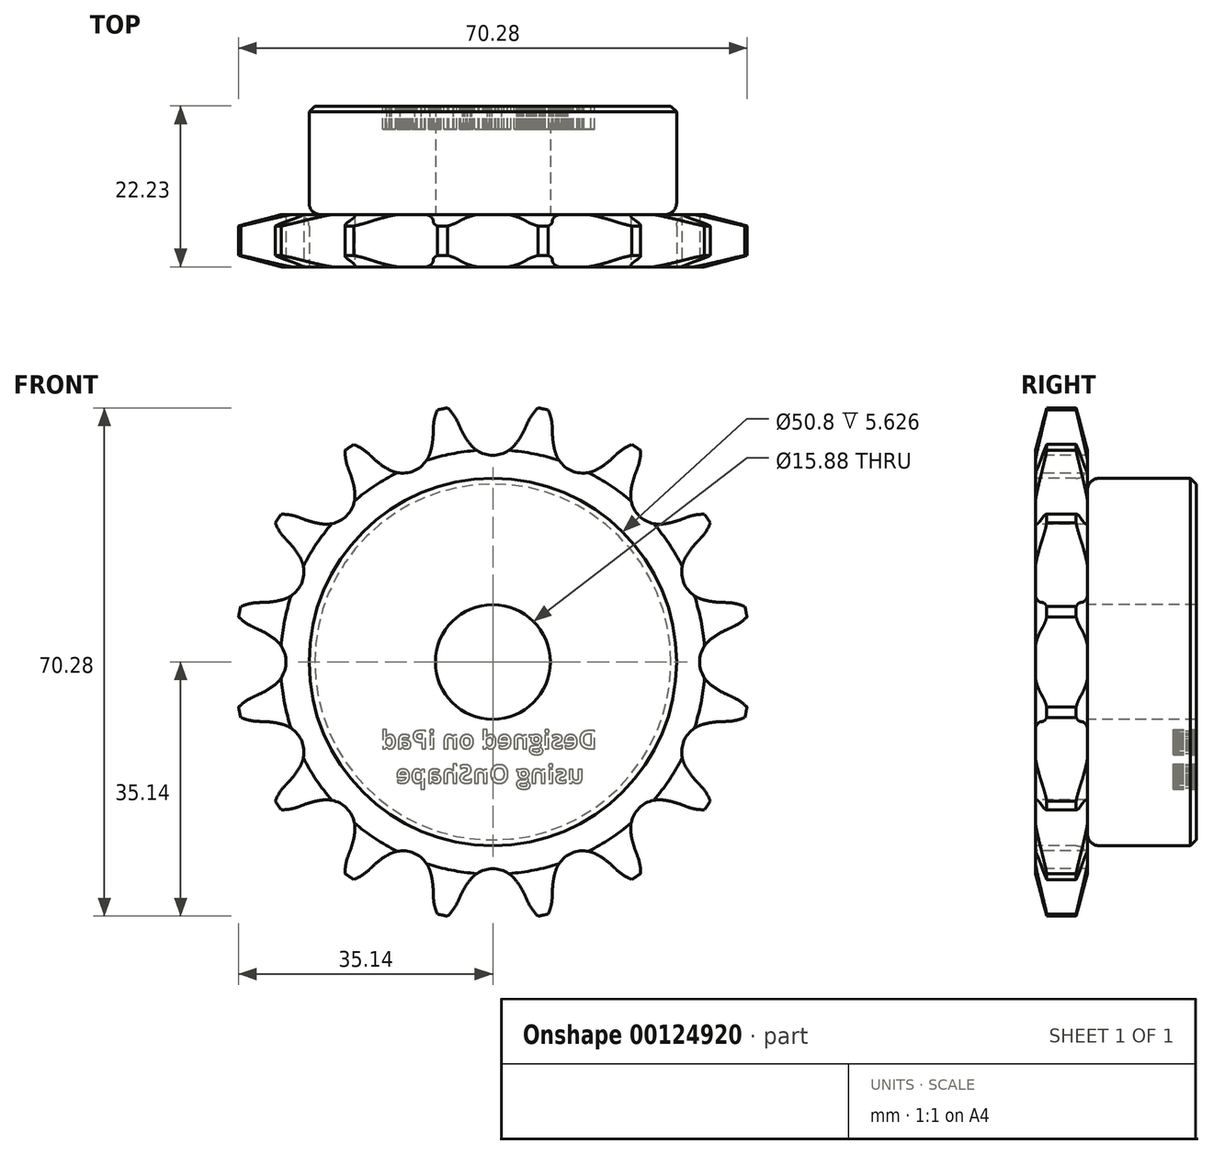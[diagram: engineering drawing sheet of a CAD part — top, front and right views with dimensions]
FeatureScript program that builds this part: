
annotation { "Feature Type Name" : "Feature", "Feature Type Description" : "" }
export const myFeature = defineFeature(function(context is Context, id is Id, definition is map)
    precondition{}
    {
        {
            var Q0;
            Q0=qCreatedBy(makeId("Right.planeOp"),FACE);
            var sketch = newSketch(context, id + "F0", { "sketchPlane" : qUnion([Q0])});
            skLineSegment(sketch, "E0", {"start": v(0, 0) * mm, "end": v(22.23, 0) * mm, "construction": true});
            skLineSegment(sketch, "E1.bottom", {"start": v(0, 7.94) * mm, "end": v(7.21, 7.94) * mm});
            skLineSegment(sketch, "E1.top", {"start": v(0, 35.69) * mm, "end": v(7.21, 35.69) * mm});
            skLineSegment(sketch, "E1.left", {"start": v(0, 7.94) * mm, "end": v(0, 35.69) * mm});
            skLineSegment(sketch, "E1.right", {"start": v(7.21, 7.94) * mm, "end": v(7.21, 35.69) * mm});
            skLineSegment(sketch, "E2.bottom", {"start": v(0, 7.94) * mm, "end": v(22.23, 7.94) * mm});
            skLineSegment(sketch, "E2.top", {"start": v(0, 25.4) * mm, "end": v(22.23, 25.4) * mm});
            skLineSegment(sketch, "E2.left", {"start": v(0, 7.94) * mm, "end": v(0, 25.4) * mm});
            skLineSegment(sketch, "E2.right", {"start": v(22.23, 7.94) * mm, "end": v(22.23, 25.4) * mm});
            skLineSegment(sketch, "E3.MirrorCS", {"start": v(0, -25.4) * mm, "end": v(22.23, -25.4) * mm});
            skLineSegment(sketch, "E4.MirrorCS", {"start": v(0, -7.94) * mm, "end": v(22.23, -7.94) * mm});
            skLineSegment(sketch, "E5.MirrorCS", {"start": v(22.23, -7.94) * mm, "end": v(22.23, -25.4) * mm});
            skLineSegment(sketch, "E6.MirrorCS", {"start": v(0, -7.94) * mm, "end": v(0, -25.4) * mm});
            skLineSegment(sketch, "E7.MirrorCS", {"start": v(0, -7.94) * mm, "end": v(0, -35.69) * mm});
            skLineSegment(sketch, "E8.MirrorCS", {"start": v(7.21, -7.94) * mm, "end": v(7.21, -35.69) * mm});
            skLineSegment(sketch, "E9.MirrorCS", {"start": v(0, -35.69) * mm, "end": v(7.21, -35.69) * mm});
            skSolve(sketch);
        }
        {
            var Q0;
            {var subQ5=sQuery(id+"F0.wireOp",EDGE,"E2.left");Q0=makeQuery(id+"F0.imprint","IMPRINT",FACE,{"disambiguationData":[TD([[makeQuery(id+"F0.imprint","IMPRINT",EDGE,{"derivedFrom":subQ5}),-1.0]])]});}
            var Q1;
            {var subQ5=sQuery(id+"F0.wireOp",EDGE,"E2.right");Q1=makeQuery(id+"F0.imprint","IMPRINT",FACE,{"disambiguationData":[TD([[makeQuery(id+"F0.imprint","IMPRINT",EDGE,{"derivedFrom":subQ5}),1.0]])]});}
            var Q2;
            {var subQ0=sQuery(id+"F0.wireOp",EDGE,"E1.top");Q2=makeQuery(id+"F0.imprint","IMPRINT",FACE,{"disambiguationData":[TD([[makeQuery(id+"F0.imprint","IMPRINT",EDGE,{"derivedFrom":subQ0}),-1.0]])]});}
            var Q3;
            Q3=sQuery(id+"F0.wireOp",EDGE,"E0");
            revolve(context, id + "F1", {"entities" : qUnion([Q0, Q1, Q2]), "axis" : qUnion([Q3]), "revolveType" : RevolveType.FULL});
        }
        {
            var Q0;
            Q0=makeQuery(id+"F1.opRevolve","SWEPT_FACE",FACE,{"disambiguationData":[OSD([sQuery(id+"F0.wireOp",EDGE,"E1.left"),sQuery(id+"F0.wireOp",EDGE,"E2.left")])]});
            var sketch = newSketch(context, id + "F2", { "sketchPlane" : qUnion([Q0])});
            skLineSegment(sketch, "E10", {"start": v(0, 32.55) * mm, "end": v(0, 0) * mm, "construction": true});
            skLineSegment(sketch, "E11", {"start": v(-4.46, 32.3) * mm, "end": v(-4.82, 33.1) * mm});
            skArc(sketch, "E12", {"start": v(-4.82, 33.1) * mm, "mid": v(-5.3, 34) * mm, "end": v(-5.94, 34.81) * mm});
            skArc(sketch, "E13", {"start": v(-5.94, 34.81) * mm, "mid": v(-6.5, 35.37) * mm, "end": v(-7.13, 35.85) * mm});
            skArc(sketch, "E14", {"start": v(-4.46, 32.3) * mm, "mid": v(-3.84, 31.14) * mm, "end": v(-3.1, 30.07) * mm});
            skArc(sketch, "E15", {"start": v(-3.1, 30.07) * mm, "mid": v(0, 28.59) * mm, "end": v(3.1, 30.07) * mm});
            skArc(sketch, "E16.MirrorCS", {"start": v(5.94, 34.81) * mm, "mid": v(6.5, 35.37) * mm, "end": v(7.13, 35.85) * mm});
            skArc(sketch, "E17.MirrorCS", {"start": v(4.82, 33.1) * mm, "mid": v(5.3, 34) * mm, "end": v(5.94, 34.81) * mm});
            skArc(sketch, "E18.MirrorCS", {"start": v(4.46, 32.3) * mm, "mid": v(3.84, 31.14) * mm, "end": v(3.1, 30.07) * mm});
            skLineSegment(sketch, "E19.MirrorCS", {"start": v(4.46, 32.3) * mm, "end": v(4.82, 33.1) * mm});
            skArc(sketch, "E20.1.0", {"start": v(8.65, 28.96) * mm, "mid": v(10.94, 26.41) * mm, "end": v(14.36, 26.6) * mm});
            skLineSegment(sketch, "E20.1.1", {"start": v(12.46, 30.07) * mm, "end": v(0, 0) * mm, "construction": true});
            skArc(sketch, "E20.1.2", {"start": v(18.8, 29.89) * mm, "mid": v(19.54, 30.19) * mm, "end": v(20.3, 30.4) * mm});
            skArc(sketch, "E20.1.3", {"start": v(8.24, 31.55) * mm, "mid": v(8.37, 30.24) * mm, "end": v(8.65, 28.96) * mm});
            skArc(sketch, "E20.1.4", {"start": v(7.84, 34.43) * mm, "mid": v(7.53, 35.16) * mm, "end": v(7.13, 35.85) * mm});
            skArc(sketch, "E20.1.5", {"start": v(8.22, 32.42) * mm, "mid": v(8.1, 33.44) * mm, "end": v(7.84, 34.43) * mm});
            skLineSegment(sketch, "E20.1.6", {"start": v(8.24, 31.55) * mm, "end": v(8.22, 32.42) * mm});
            skLineSegment(sketch, "E20.1.7", {"start": v(16.48, 28.14) * mm, "end": v(17.12, 28.74) * mm});
            skArc(sketch, "E20.1.8", {"start": v(16.48, 28.14) * mm, "mid": v(15.47, 27.3) * mm, "end": v(14.36, 26.6) * mm});
            skArc(sketch, "E20.1.9", {"start": v(17.12, 28.74) * mm, "mid": v(17.92, 29.38) * mm, "end": v(18.8, 29.89) * mm});
            skArc(sketch, "E20.2.0", {"start": v(19.08, 23.45) * mm, "mid": v(20.21, 20.21) * mm, "end": v(23.45, 19.08) * mm});
            skLineSegment(sketch, "E20.2.1", {"start": v(23.02, 23.02) * mm, "end": v(0, 0) * mm, "construction": true});
            skArc(sketch, "E20.2.2", {"start": v(28.81, 20.42) * mm, "mid": v(29.6, 20.4) * mm, "end": v(30.4, 20.3) * mm});
            skArc(sketch, "E20.2.3", {"start": v(19.69, 26) * mm, "mid": v(19.3, 24.74) * mm, "end": v(19.08, 23.45) * mm});
            skArc(sketch, "E20.2.4", {"start": v(20.42, 28.81) * mm, "mid": v(20.4, 29.6) * mm, "end": v(20.3, 30.4) * mm});
            skArc(sketch, "E20.2.5", {"start": v(20, 26.8) * mm, "mid": v(20.29, 27.8) * mm, "end": v(20.42, 28.81) * mm});
            skLineSegment(sketch, "E20.2.6", {"start": v(19.69, 26) * mm, "end": v(20, 26.8) * mm});
            skLineSegment(sketch, "E20.2.7", {"start": v(26, 19.69) * mm, "end": v(26.8, 20) * mm});
            skArc(sketch, "E20.2.8", {"start": v(26, 19.69) * mm, "mid": v(24.74, 19.3) * mm, "end": v(23.45, 19.08) * mm});
            skArc(sketch, "E20.2.9", {"start": v(26.8, 20) * mm, "mid": v(27.8, 20.29) * mm, "end": v(28.81, 20.42) * mm});
            skArc(sketch, "E20.3.0", {"start": v(26.6, 14.36) * mm, "mid": v(26.41, 10.94) * mm, "end": v(28.96, 8.65) * mm});
            skLineSegment(sketch, "E20.3.1", {"start": v(30.07, 12.46) * mm, "end": v(0, 0) * mm, "construction": true});
            skArc(sketch, "E20.3.2", {"start": v(34.43, 7.84) * mm, "mid": v(35.16, 7.53) * mm, "end": v(35.85, 7.13) * mm});
            skArc(sketch, "E20.3.3", {"start": v(28.14, 16.48) * mm, "mid": v(27.3, 15.47) * mm, "end": v(26.6, 14.36) * mm});
            skArc(sketch, "E20.3.4", {"start": v(29.89, 18.8) * mm, "mid": v(30.19, 19.54) * mm, "end": v(30.4, 20.3) * mm});
            skArc(sketch, "E20.3.5", {"start": v(28.74, 17.12) * mm, "mid": v(29.38, 17.92) * mm, "end": v(29.89, 18.8) * mm});
            skLineSegment(sketch, "E20.3.6", {"start": v(28.14, 16.48) * mm, "end": v(28.74, 17.12) * mm});
            skLineSegment(sketch, "E20.3.7", {"start": v(31.55, 8.24) * mm, "end": v(32.42, 8.22) * mm});
            skArc(sketch, "E20.3.8", {"start": v(31.55, 8.24) * mm, "mid": v(30.24, 8.37) * mm, "end": v(28.96, 8.65) * mm});
            skArc(sketch, "E20.3.9", {"start": v(32.42, 8.22) * mm, "mid": v(33.44, 8.1) * mm, "end": v(34.43, 7.84) * mm});
            skArc(sketch, "E20.4.0", {"start": v(30.07, 3.1) * mm, "mid": v(28.59, 0) * mm, "end": v(30.07, -3.1) * mm});
            skLineSegment(sketch, "E20.4.1", {"start": v(32.55, 0) * mm, "end": v(0, 0) * mm, "construction": true});
            skArc(sketch, "E20.4.2", {"start": v(34.81, -5.94) * mm, "mid": v(35.37, -6.5) * mm, "end": v(35.85, -7.13) * mm});
            skArc(sketch, "E20.4.3", {"start": v(32.3, 4.46) * mm, "mid": v(31.14, 3.84) * mm, "end": v(30.07, 3.1) * mm});
            skArc(sketch, "E20.4.4", {"start": v(34.81, 5.94) * mm, "mid": v(35.37, 6.5) * mm, "end": v(35.85, 7.13) * mm});
            skArc(sketch, "E20.4.5", {"start": v(33.1, 4.82) * mm, "mid": v(34, 5.3) * mm, "end": v(34.81, 5.94) * mm});
            skLineSegment(sketch, "E20.4.6", {"start": v(32.3, 4.46) * mm, "end": v(33.1, 4.82) * mm});
            skLineSegment(sketch, "E20.4.7", {"start": v(32.3, -4.46) * mm, "end": v(33.1, -4.82) * mm});
            skArc(sketch, "E20.4.8", {"start": v(32.3, -4.46) * mm, "mid": v(31.14, -3.84) * mm, "end": v(30.07, -3.1) * mm});
            skArc(sketch, "E20.4.9", {"start": v(33.1, -4.82) * mm, "mid": v(34, -5.3) * mm, "end": v(34.81, -5.94) * mm});
            skArc(sketch, "E20.5.0", {"start": v(28.96, -8.65) * mm, "mid": v(26.41, -10.94) * mm, "end": v(26.6, -14.36) * mm});
            skLineSegment(sketch, "E20.5.1", {"start": v(30.07, -12.46) * mm, "end": v(0, 0) * mm, "construction": true});
            skArc(sketch, "E20.5.2", {"start": v(29.89, -18.8) * mm, "mid": v(30.19, -19.54) * mm, "end": v(30.4, -20.3) * mm});
            skArc(sketch, "E20.5.3", {"start": v(31.55, -8.24) * mm, "mid": v(30.24, -8.37) * mm, "end": v(28.96, -8.65) * mm});
            skArc(sketch, "E20.5.4", {"start": v(34.43, -7.84) * mm, "mid": v(35.16, -7.53) * mm, "end": v(35.85, -7.13) * mm});
            skArc(sketch, "E20.5.5", {"start": v(32.42, -8.22) * mm, "mid": v(33.44, -8.1) * mm, "end": v(34.43, -7.84) * mm});
            skLineSegment(sketch, "E20.5.6", {"start": v(31.55, -8.24) * mm, "end": v(32.42, -8.22) * mm});
            skLineSegment(sketch, "E20.5.7", {"start": v(28.14, -16.48) * mm, "end": v(28.74, -17.12) * mm});
            skArc(sketch, "E20.5.8", {"start": v(28.14, -16.48) * mm, "mid": v(27.3, -15.47) * mm, "end": v(26.6, -14.36) * mm});
            skArc(sketch, "E20.5.9", {"start": v(28.74, -17.12) * mm, "mid": v(29.38, -17.92) * mm, "end": v(29.89, -18.8) * mm});
            skArc(sketch, "E20.6.0", {"start": v(23.45, -19.08) * mm, "mid": v(20.21, -20.21) * mm, "end": v(19.08, -23.45) * mm});
            skLineSegment(sketch, "E20.6.1", {"start": v(23.02, -23.02) * mm, "end": v(0, 0) * mm, "construction": true});
            skArc(sketch, "E20.6.2", {"start": v(20.42, -28.81) * mm, "mid": v(20.4, -29.6) * mm, "end": v(20.3, -30.4) * mm});
            skArc(sketch, "E20.6.3", {"start": v(26, -19.69) * mm, "mid": v(24.74, -19.3) * mm, "end": v(23.45, -19.08) * mm});
            skArc(sketch, "E20.6.4", {"start": v(28.81, -20.42) * mm, "mid": v(29.6, -20.4) * mm, "end": v(30.4, -20.3) * mm});
            skArc(sketch, "E20.6.5", {"start": v(26.8, -20) * mm, "mid": v(27.8, -20.29) * mm, "end": v(28.81, -20.42) * mm});
            skLineSegment(sketch, "E20.6.6", {"start": v(26, -19.69) * mm, "end": v(26.8, -20) * mm});
            skLineSegment(sketch, "E20.6.7", {"start": v(19.69, -26) * mm, "end": v(20, -26.8) * mm});
            skArc(sketch, "E20.6.8", {"start": v(19.69, -26) * mm, "mid": v(19.3, -24.74) * mm, "end": v(19.08, -23.45) * mm});
            skArc(sketch, "E20.6.9", {"start": v(20, -26.8) * mm, "mid": v(20.29, -27.8) * mm, "end": v(20.42, -28.81) * mm});
            skArc(sketch, "E20.7.0", {"start": v(14.36, -26.6) * mm, "mid": v(10.94, -26.41) * mm, "end": v(8.65, -28.96) * mm});
            skLineSegment(sketch, "E20.7.1", {"start": v(12.46, -30.07) * mm, "end": v(0, 0) * mm, "construction": true});
            skArc(sketch, "E20.7.2", {"start": v(7.84, -34.43) * mm, "mid": v(7.53, -35.16) * mm, "end": v(7.13, -35.85) * mm});
            skArc(sketch, "E20.7.3", {"start": v(16.48, -28.14) * mm, "mid": v(15.47, -27.3) * mm, "end": v(14.36, -26.6) * mm});
            skArc(sketch, "E20.7.4", {"start": v(18.8, -29.89) * mm, "mid": v(19.54, -30.19) * mm, "end": v(20.3, -30.4) * mm});
            skArc(sketch, "E20.7.5", {"start": v(17.12, -28.74) * mm, "mid": v(17.92, -29.38) * mm, "end": v(18.8, -29.89) * mm});
            skLineSegment(sketch, "E20.7.6", {"start": v(16.48, -28.14) * mm, "end": v(17.12, -28.74) * mm});
            skLineSegment(sketch, "E20.7.7", {"start": v(8.24, -31.55) * mm, "end": v(8.22, -32.42) * mm});
            skArc(sketch, "E20.7.8", {"start": v(8.24, -31.55) * mm, "mid": v(8.37, -30.24) * mm, "end": v(8.65, -28.96) * mm});
            skArc(sketch, "E20.7.9", {"start": v(8.22, -32.42) * mm, "mid": v(8.1, -33.44) * mm, "end": v(7.84, -34.43) * mm});
            skArc(sketch, "E20.8.0", {"start": v(3.1, -30.07) * mm, "mid": v(0, -28.59) * mm, "end": v(-3.1, -30.07) * mm});
            skLineSegment(sketch, "E20.8.1", {"start": v(0, -32.55) * mm, "end": v(0, 0) * mm, "construction": true});
            skArc(sketch, "E20.8.2", {"start": v(-5.94, -34.81) * mm, "mid": v(-6.5, -35.37) * mm, "end": v(-7.13, -35.85) * mm});
            skArc(sketch, "E20.8.3", {"start": v(4.46, -32.3) * mm, "mid": v(3.84, -31.14) * mm, "end": v(3.1, -30.07) * mm});
            skArc(sketch, "E20.8.4", {"start": v(5.94, -34.81) * mm, "mid": v(6.5, -35.37) * mm, "end": v(7.13, -35.85) * mm});
            skArc(sketch, "E20.8.5", {"start": v(4.82, -33.1) * mm, "mid": v(5.3, -34) * mm, "end": v(5.94, -34.81) * mm});
            skLineSegment(sketch, "E20.8.6", {"start": v(4.46, -32.3) * mm, "end": v(4.82, -33.1) * mm});
            skLineSegment(sketch, "E20.8.7", {"start": v(-4.46, -32.3) * mm, "end": v(-4.82, -33.1) * mm});
            skArc(sketch, "E20.8.8", {"start": v(-4.46, -32.3) * mm, "mid": v(-3.84, -31.14) * mm, "end": v(-3.1, -30.07) * mm});
            skArc(sketch, "E20.8.9", {"start": v(-4.82, -33.1) * mm, "mid": v(-5.3, -34) * mm, "end": v(-5.94, -34.81) * mm});
            skArc(sketch, "E20.9.0", {"start": v(-8.65, -28.96) * mm, "mid": v(-10.94, -26.41) * mm, "end": v(-14.36, -26.6) * mm});
            skLineSegment(sketch, "E20.9.1", {"start": v(-12.46, -30.07) * mm, "end": v(0, 0) * mm, "construction": true});
            skArc(sketch, "E20.9.2", {"start": v(-18.8, -29.89) * mm, "mid": v(-19.54, -30.19) * mm, "end": v(-20.3, -30.4) * mm});
            skArc(sketch, "E20.9.3", {"start": v(-8.24, -31.55) * mm, "mid": v(-8.37, -30.24) * mm, "end": v(-8.65, -28.96) * mm});
            skArc(sketch, "E20.9.4", {"start": v(-7.84, -34.43) * mm, "mid": v(-7.53, -35.16) * mm, "end": v(-7.13, -35.85) * mm});
            skArc(sketch, "E20.9.5", {"start": v(-8.22, -32.42) * mm, "mid": v(-8.1, -33.44) * mm, "end": v(-7.84, -34.43) * mm});
            skLineSegment(sketch, "E20.9.6", {"start": v(-8.24, -31.55) * mm, "end": v(-8.22, -32.42) * mm});
            skLineSegment(sketch, "E20.9.7", {"start": v(-16.48, -28.14) * mm, "end": v(-17.12, -28.74) * mm});
            skArc(sketch, "E20.9.8", {"start": v(-16.48, -28.14) * mm, "mid": v(-15.47, -27.3) * mm, "end": v(-14.36, -26.6) * mm});
            skArc(sketch, "E20.9.9", {"start": v(-17.12, -28.74) * mm, "mid": v(-17.92, -29.38) * mm, "end": v(-18.8, -29.89) * mm});
            skArc(sketch, "E20.10.0", {"start": v(-19.08, -23.45) * mm, "mid": v(-20.21, -20.21) * mm, "end": v(-23.45, -19.08) * mm});
            skLineSegment(sketch, "E20.10.1", {"start": v(-23.02, -23.02) * mm, "end": v(0, 0) * mm, "construction": true});
            skArc(sketch, "E20.10.2", {"start": v(-28.81, -20.42) * mm, "mid": v(-29.6, -20.4) * mm, "end": v(-30.4, -20.3) * mm});
            skArc(sketch, "E20.10.3", {"start": v(-19.69, -26) * mm, "mid": v(-19.3, -24.74) * mm, "end": v(-19.08, -23.45) * mm});
            skArc(sketch, "E20.10.4", {"start": v(-20.42, -28.81) * mm, "mid": v(-20.4, -29.6) * mm, "end": v(-20.3, -30.4) * mm});
            skArc(sketch, "E20.10.5", {"start": v(-20, -26.8) * mm, "mid": v(-20.29, -27.8) * mm, "end": v(-20.42, -28.81) * mm});
            skLineSegment(sketch, "E20.10.6", {"start": v(-19.69, -26) * mm, "end": v(-20, -26.8) * mm});
            skLineSegment(sketch, "E20.10.7", {"start": v(-26, -19.69) * mm, "end": v(-26.8, -20) * mm});
            skArc(sketch, "E20.10.8", {"start": v(-26, -19.69) * mm, "mid": v(-24.74, -19.3) * mm, "end": v(-23.45, -19.08) * mm});
            skArc(sketch, "E20.10.9", {"start": v(-26.8, -20) * mm, "mid": v(-27.8, -20.29) * mm, "end": v(-28.81, -20.42) * mm});
            skArc(sketch, "E20.11.0", {"start": v(-26.6, -14.36) * mm, "mid": v(-26.41, -10.94) * mm, "end": v(-28.96, -8.65) * mm});
            skLineSegment(sketch, "E20.11.1", {"start": v(-30.07, -12.46) * mm, "end": v(0, 0) * mm, "construction": true});
            skArc(sketch, "E20.11.2", {"start": v(-34.43, -7.84) * mm, "mid": v(-35.16, -7.53) * mm, "end": v(-35.85, -7.13) * mm});
            skArc(sketch, "E20.11.3", {"start": v(-28.14, -16.48) * mm, "mid": v(-27.3, -15.47) * mm, "end": v(-26.6, -14.36) * mm});
            skArc(sketch, "E20.11.4", {"start": v(-29.89, -18.8) * mm, "mid": v(-30.19, -19.54) * mm, "end": v(-30.4, -20.3) * mm});
            skArc(sketch, "E20.11.5", {"start": v(-28.74, -17.12) * mm, "mid": v(-29.38, -17.92) * mm, "end": v(-29.89, -18.8) * mm});
            skLineSegment(sketch, "E20.11.6", {"start": v(-28.14, -16.48) * mm, "end": v(-28.74, -17.12) * mm});
            skLineSegment(sketch, "E20.11.7", {"start": v(-31.55, -8.24) * mm, "end": v(-32.42, -8.22) * mm});
            skArc(sketch, "E20.11.8", {"start": v(-31.55, -8.24) * mm, "mid": v(-30.24, -8.37) * mm, "end": v(-28.96, -8.65) * mm});
            skArc(sketch, "E20.11.9", {"start": v(-32.42, -8.22) * mm, "mid": v(-33.44, -8.1) * mm, "end": v(-34.43, -7.84) * mm});
            skArc(sketch, "E20.12.0", {"start": v(-30.07, -3.1) * mm, "mid": v(-28.59, 0) * mm, "end": v(-30.07, 3.1) * mm});
            skLineSegment(sketch, "E20.12.1", {"start": v(-32.55, 0) * mm, "end": v(0, 0) * mm, "construction": true});
            skArc(sketch, "E20.12.2", {"start": v(-34.81, 5.94) * mm, "mid": v(-35.37, 6.5) * mm, "end": v(-35.85, 7.13) * mm});
            skArc(sketch, "E20.12.3", {"start": v(-32.3, -4.46) * mm, "mid": v(-31.14, -3.84) * mm, "end": v(-30.07, -3.1) * mm});
            skArc(sketch, "E20.12.4", {"start": v(-34.81, -5.94) * mm, "mid": v(-35.37, -6.5) * mm, "end": v(-35.85, -7.13) * mm});
            skArc(sketch, "E20.12.5", {"start": v(-33.1, -4.82) * mm, "mid": v(-34, -5.3) * mm, "end": v(-34.81, -5.94) * mm});
            skLineSegment(sketch, "E20.12.6", {"start": v(-32.3, -4.46) * mm, "end": v(-33.1, -4.82) * mm});
            skLineSegment(sketch, "E20.12.7", {"start": v(-32.3, 4.46) * mm, "end": v(-33.1, 4.82) * mm});
            skArc(sketch, "E20.12.8", {"start": v(-32.3, 4.46) * mm, "mid": v(-31.14, 3.84) * mm, "end": v(-30.07, 3.1) * mm});
            skArc(sketch, "E20.12.9", {"start": v(-33.1, 4.82) * mm, "mid": v(-34, 5.3) * mm, "end": v(-34.81, 5.94) * mm});
            skArc(sketch, "E20.13.0", {"start": v(-28.96, 8.65) * mm, "mid": v(-26.41, 10.94) * mm, "end": v(-26.6, 14.36) * mm});
            skLineSegment(sketch, "E20.13.1", {"start": v(-30.07, 12.46) * mm, "end": v(0, 0) * mm, "construction": true});
            skArc(sketch, "E20.13.2", {"start": v(-29.89, 18.8) * mm, "mid": v(-30.19, 19.54) * mm, "end": v(-30.4, 20.3) * mm});
            skArc(sketch, "E20.13.3", {"start": v(-31.55, 8.24) * mm, "mid": v(-30.24, 8.37) * mm, "end": v(-28.96, 8.65) * mm});
            skArc(sketch, "E20.13.4", {"start": v(-34.43, 7.84) * mm, "mid": v(-35.16, 7.53) * mm, "end": v(-35.85, 7.13) * mm});
            skArc(sketch, "E20.13.5", {"start": v(-32.42, 8.22) * mm, "mid": v(-33.44, 8.1) * mm, "end": v(-34.43, 7.84) * mm});
            skLineSegment(sketch, "E20.13.6", {"start": v(-31.55, 8.24) * mm, "end": v(-32.42, 8.22) * mm});
            skLineSegment(sketch, "E20.13.7", {"start": v(-28.14, 16.48) * mm, "end": v(-28.74, 17.12) * mm});
            skArc(sketch, "E20.13.8", {"start": v(-28.14, 16.48) * mm, "mid": v(-27.3, 15.47) * mm, "end": v(-26.6, 14.36) * mm});
            skArc(sketch, "E20.13.9", {"start": v(-28.74, 17.12) * mm, "mid": v(-29.38, 17.92) * mm, "end": v(-29.89, 18.8) * mm});
            skArc(sketch, "E20.14.0", {"start": v(-23.45, 19.08) * mm, "mid": v(-20.21, 20.21) * mm, "end": v(-19.08, 23.45) * mm});
            skLineSegment(sketch, "E20.14.1", {"start": v(-23.02, 23.02) * mm, "end": v(0, 0) * mm, "construction": true});
            skArc(sketch, "E20.14.2", {"start": v(-20.42, 28.81) * mm, "mid": v(-20.4, 29.6) * mm, "end": v(-20.3, 30.4) * mm});
            skArc(sketch, "E20.14.3", {"start": v(-26, 19.69) * mm, "mid": v(-24.74, 19.3) * mm, "end": v(-23.45, 19.08) * mm});
            skArc(sketch, "E20.14.4", {"start": v(-28.81, 20.42) * mm, "mid": v(-29.6, 20.4) * mm, "end": v(-30.4, 20.3) * mm});
            skArc(sketch, "E20.14.5", {"start": v(-26.8, 20) * mm, "mid": v(-27.8, 20.29) * mm, "end": v(-28.81, 20.42) * mm});
            skLineSegment(sketch, "E20.14.6", {"start": v(-26, 19.69) * mm, "end": v(-26.8, 20) * mm});
            skLineSegment(sketch, "E20.14.7", {"start": v(-19.69, 26) * mm, "end": v(-20, 26.8) * mm});
            skArc(sketch, "E20.14.8", {"start": v(-19.69, 26) * mm, "mid": v(-19.3, 24.74) * mm, "end": v(-19.08, 23.45) * mm});
            skArc(sketch, "E20.14.9", {"start": v(-20, 26.8) * mm, "mid": v(-20.29, 27.8) * mm, "end": v(-20.42, 28.81) * mm});
            skArc(sketch, "E20.15.0", {"start": v(-14.36, 26.6) * mm, "mid": v(-10.94, 26.41) * mm, "end": v(-8.65, 28.96) * mm});
            skLineSegment(sketch, "E20.15.1", {"start": v(-12.46, 30.07) * mm, "end": v(0, 0) * mm, "construction": true});
            skArc(sketch, "E20.15.2", {"start": v(-7.84, 34.43) * mm, "mid": v(-7.53, 35.16) * mm, "end": v(-7.13, 35.85) * mm});
            skArc(sketch, "E20.15.3", {"start": v(-16.48, 28.14) * mm, "mid": v(-15.47, 27.3) * mm, "end": v(-14.36, 26.6) * mm});
            skArc(sketch, "E20.15.4", {"start": v(-18.8, 29.89) * mm, "mid": v(-19.54, 30.19) * mm, "end": v(-20.3, 30.4) * mm});
            skArc(sketch, "E20.15.5", {"start": v(-17.12, 28.74) * mm, "mid": v(-17.92, 29.38) * mm, "end": v(-18.8, 29.89) * mm});
            skLineSegment(sketch, "E20.15.6", {"start": v(-16.48, 28.14) * mm, "end": v(-17.12, 28.74) * mm});
            skLineSegment(sketch, "E20.15.7", {"start": v(-8.24, 31.55) * mm, "end": v(-8.22, 32.42) * mm});
            skArc(sketch, "E20.15.8", {"start": v(-8.24, 31.55) * mm, "mid": v(-8.37, 30.24) * mm, "end": v(-8.65, 28.96) * mm});
            skArc(sketch, "E20.15.9", {"start": v(-8.22, 32.42) * mm, "mid": v(-8.1, 33.44) * mm, "end": v(-7.84, 34.43) * mm});
            skPoint(sketch, "E20.center", {"position": v(0, 0) * mm});
            skLineSegment(sketch, "E20.anchor1", {"start": v(0, 0) * mm, "end": v(0, 0) * mm});
            skLineSegment(sketch, "E20.anchor2", {"start": v(0, 0) * mm, "end": v(0, 0) * mm});
            skSolve(sketch);
        }
        {
            var Q0;
            Q0=makeQuery(id+"F1.opRevolve","SWEPT_EDGE",EDGE,{"disambiguationData":[OSD([sQuery(id+"F0.wireOp",EDGE,"E1.right"),sQuery(id+"F0.wireOp",EDGE,"E2.top")])]});
            fillet(context, id + "F3", {"entities" : qUnion([Q0]), "radius" : 1.59 * mm, "tangentPropagation" : true, "allowEdgeOverflow" : false});
        }
        {
            var Q0;
            Q0=makeQuery(id+"F1.opRevolve","SWEPT_EDGE",EDGE,{"disambiguationData":[OSD([sQuery(id+"F0.wireOp",EDGE,"E2.top"),sQuery(id+"F0.wireOp",EDGE,"E2.right")])]});
            chamfer(context, id + "F4", {"entities" : qUnion([Q0]), "width" : 0.8 * mm, "tangentPropagation" : true});
        }
        {
            var Q0;
            Q0=makeQuery(id+"F1.opRevolve","SWEPT_EDGE",EDGE,{"disambiguationData":[OSD([sQuery(id+"F0.wireOp",EDGE,"E1.top"),sQuery(id+"F0.wireOp",EDGE,"E1.left")])]});
            var Q1;
            Q1=makeQuery(id+"F1.opRevolve","SWEPT_EDGE",EDGE,{"disambiguationData":[OSD([sQuery(id+"F0.wireOp",EDGE,"E1.top"),sQuery(id+"F0.wireOp",EDGE,"E1.right")])]});
            chamfer(context, id + "F5", {"entities" : qUnion([Q0, Q1]), "chamferType" : ChamferType.TWO_OFFSETS, "width1" : 6.35 * mm, "oppositeDirection" : false, "width2" : 1.57 * mm, "tangentPropagation" : true});
        }
        {
            var Q0;
            Q0 = qSketchRegion(id + "F2", true);
            extrude(context, id + "F6", {"entities" : qUnion([Q0]), "operationType" : NewBodyOperationType.INTERSECT, "oppositeDirection" : true, "depth" : 25.4 * mm});
        }
        {
            var Q0;
            Q0=makeQuery(id+"F1.opRevolve","SWEPT_FACE",FACE,{"disambiguationData":[OSD([sQuery(id+"F0.wireOp",EDGE,"E2.right")])]});
            var sketch = newSketch(context, id + "F7", { "sketchPlane" : qUnion([Q0])});
            skText(sketch, "E21", { "text": "Designed on iPad\n  using OnShape", "fontName": "OpenSans-Bold.ttf"});
            const initialGuessF7  = {"E21": [-0.01441, -0.01198, 1, 0, 0.00252]};
            skSetInitialGuess(sketch, initialGuessF7);
            skSolve(sketch);
        }
        {
            var Q0;
            Q0 = qSketchRegion(id + "F7", true);
            extrude(context, id + "F8", {"entities" : qUnion([Q0]), "operationType" : NewBodyOperationType.REMOVE, "oppositeDirection" : true, "depth" : 3.17 * mm});
        }
    });
